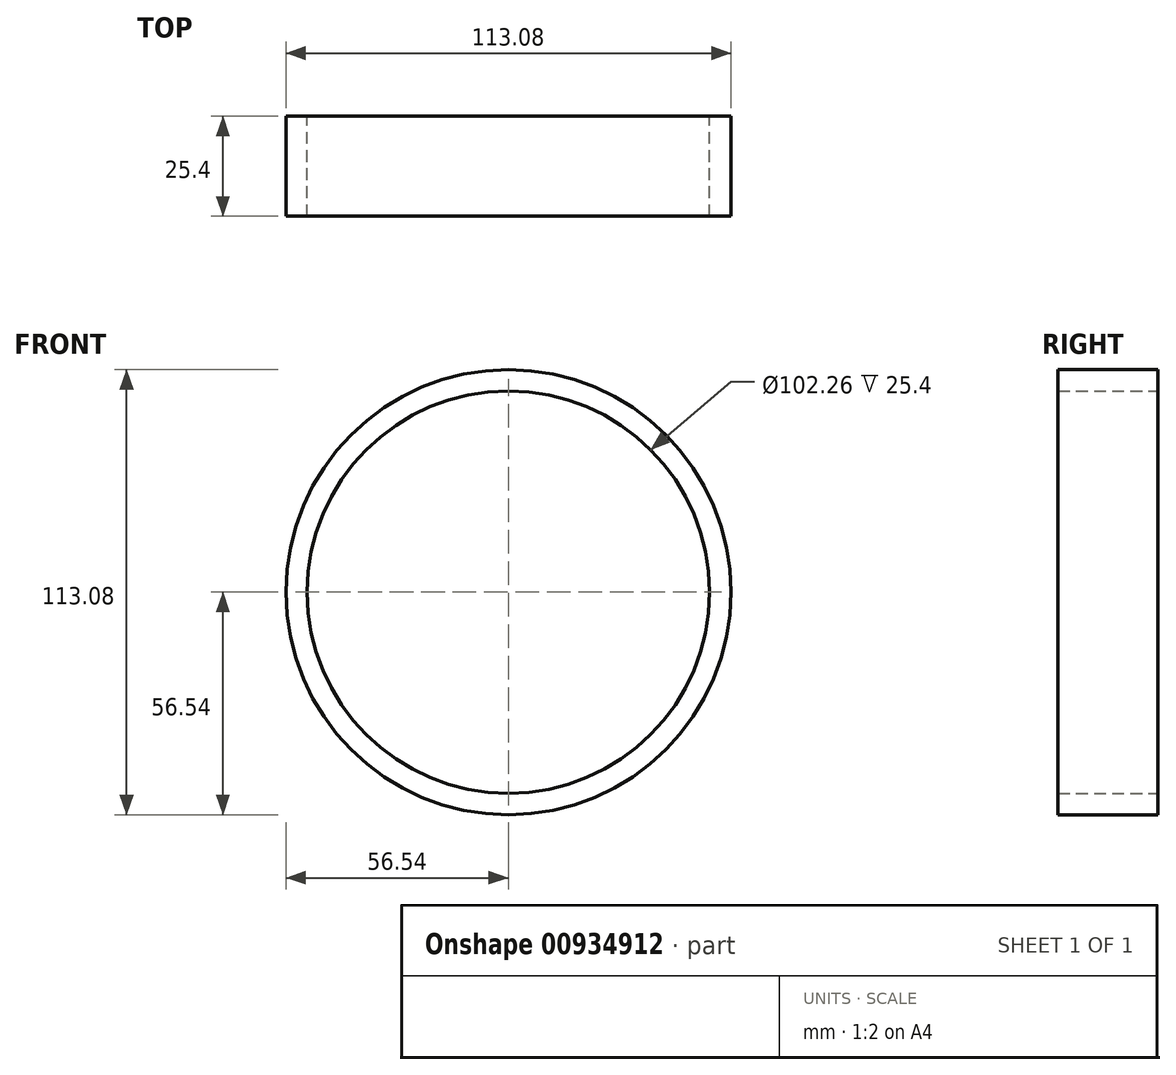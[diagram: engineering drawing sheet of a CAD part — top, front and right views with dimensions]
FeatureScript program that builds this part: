
annotation { "Feature Type Name" : "Feature", "Feature Type Description" : "" }
export const myFeature = defineFeature(function(context is Context, id is Id, definition is map)
    precondition{}
    {
        {
            var Q0;
            Q0=qCreatedBy(makeId("Front.planeOp"),FACE);
            var sketch = newSketch(context, id + "F0", { "sketchPlane" : qUnion([Q0])});
            skCircle(sketch, "E0", {"center": v(0, 0) * mm, "radius": 56.54 * mm});
            skSolve(sketch);
        }
        {
            var Q0;
            Q0=qCreatedBy(makeId("Front.planeOp"),FACE);
            var sketch = newSketch(context, id + "F1", { "sketchPlane" : qUnion([Q0])});
            skCircle(sketch, "E1", {"center": v(0, 0) * mm, "radius": 51.76 * mm});
            skSolve(sketch);
        }
        {
            var Q0;
            Q0=makeQuery(id+"F0.imprint","IMPRINT",FACE,{"disambiguationData":[TD([[makeQuery(id+"F0.imprint","IMPRINT",EDGE,{"derivedFrom":sQuery(id+"F0.wireOp",EDGE,"E0")}),1.0]])]});
            var Q1;
            Q1=sQuery(id+"F1.wireOp",EDGE,"E1");
            var Q2;
            Q2=sQuery(id+"F0.wireOp",EDGE,"E0");
            extrude(context, id + "F2", {"entities" : qUnion([Q0]), "surfaceEntities" : qUnion([Q1, Q2]), "depth" : 25.4 * mm, "offsetDistance" : 25.4 * mm});
        }
        {
            var Q0;
            Q0=makeQuery(id+"F2.opExtrude","CAP_FACE",FACE,{"disambiguationData":[OSD([sQuery(id+"F0.wireOp",EDGE,"E0")])],"isStart":true});
            var sketch = newSketch(context, id + "F3", { "sketchPlane" : qUnion([Q0])});
            skCircle(sketch, "E2", {"center": v(0, 0) * mm, "radius": 51.13 * mm});
            skSolve(sketch);
        }
        {
            var Q0;
            Q0=makeQuery(id+"F3.imprint","IMPRINT",FACE,{"disambiguationData":[TD([[makeQuery(id+"F3.imprint","IMPRINT",EDGE,{"derivedFrom":sQuery(id+"F3.wireOp",EDGE,"E2")}),1.0]])]});
            var Q1;
            Q1 = qSketchRegion(id + "F3", true);
            extrude(context, id + "F4", {"entities" : qUnion([Q0, Q1]), "operationType" : NewBodyOperationType.REMOVE, "oppositeDirection" : true, "depth" : 25.4 * mm, "offsetDistance" : 25.4 * mm});
        }
    });
